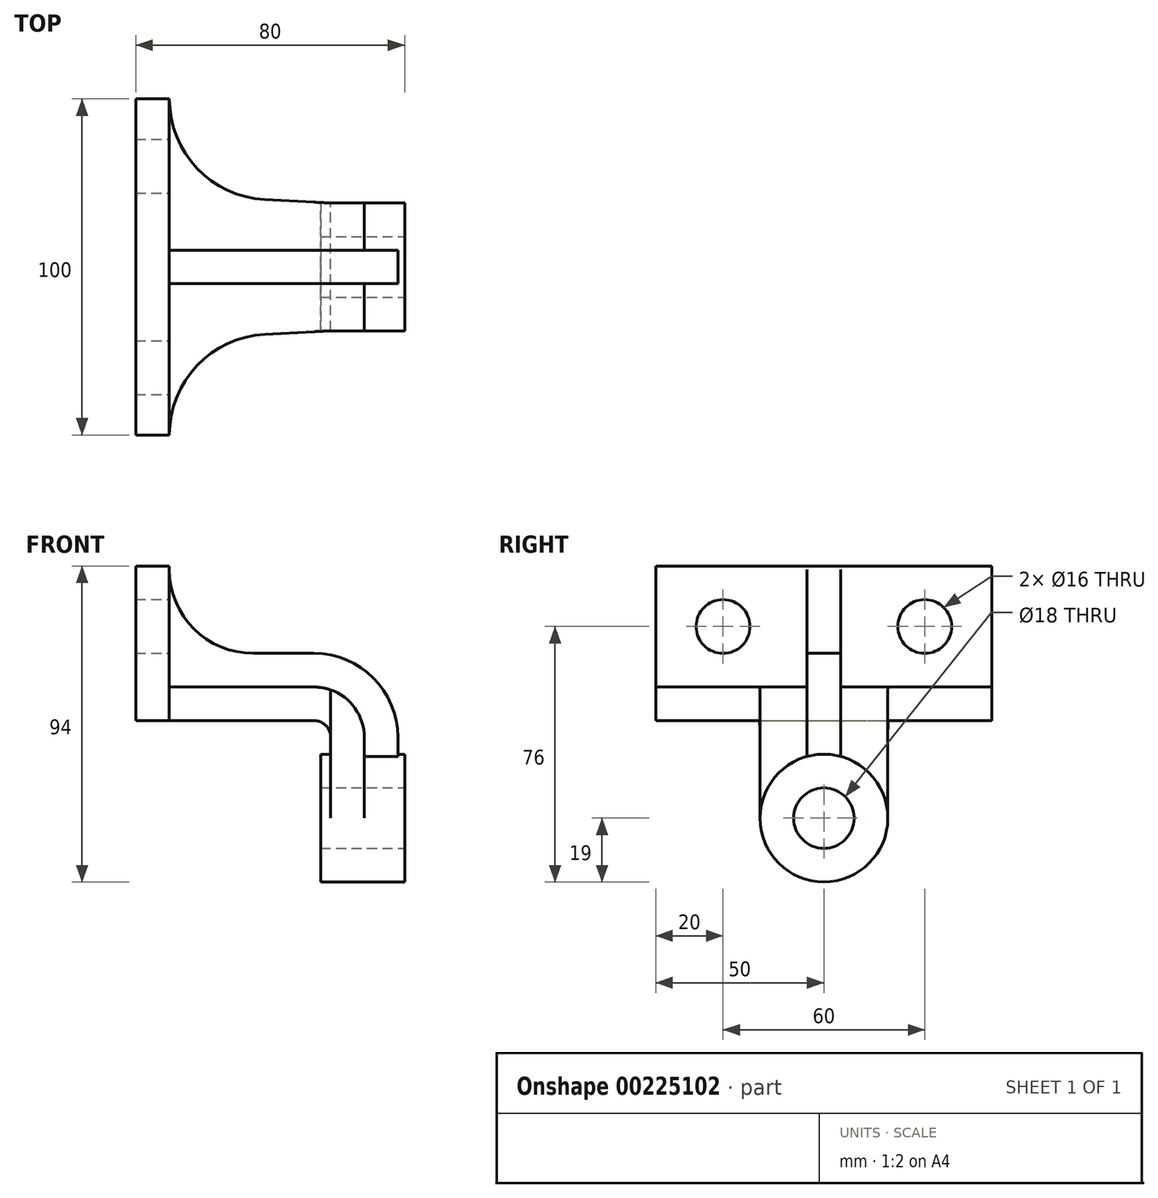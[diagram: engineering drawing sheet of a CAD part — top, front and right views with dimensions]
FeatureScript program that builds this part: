
annotation { "Feature Type Name" : "Feature", "Feature Type Description" : "" }
export const myFeature = defineFeature(function(context is Context, id is Id, definition is map)
    precondition{}
    {
        {
            var Q0;
            Q0=qCreatedBy(makeId("Front.planeOp"),FACE);
            var sketch = newSketch(context, id + "F0", { "sketchPlane" : qUnion([Q0])});
            skLineSegment(sketch, "E0", {"start": v(0, 0) * mm, "end": v(0, 46) * mm});
            skLineSegment(sketch, "E1", {"start": v(0, 46) * mm, "end": v(10, 46) * mm});
            skLineSegment(sketch, "E2", {"start": v(10, 46) * mm, "end": v(10, 10) * mm});
            skLineSegment(sketch, "E3", {"start": v(10, 10) * mm, "end": v(58, 10) * mm});
            skLineSegment(sketch, "E4", {"start": v(58, 10) * mm, "end": v(68, 10) * mm});
            skLineSegment(sketch, "E5", {"start": v(68, 10) * mm, "end": v(68, -29) * mm});
            skLineSegment(sketch, "E6", {"start": v(68, -29) * mm, "end": v(58, -29) * mm});
            skLineSegment(sketch, "E7", {"start": v(58, -29) * mm, "end": v(58, 10) * mm});
            skLineSegment(sketch, "E8", {"start": v(0, 0) * mm, "end": v(58, 0) * mm});
            skSolve(sketch);
        }
        {
            var Q0;
            Q0=makeQuery(id+"F0.imprint","IMPRINT",FACE,{"disambiguationData":[TD([[makeQuery(id+"F0.imprint","IMPRINT",EDGE,{"derivedFrom":sQuery(id+"F0.wireOp",EDGE,"E0")}),-1.0]])]});
            extrude(context, id + "F1", {"entities" : qUnion([Q0]), "endBound" : BoundingType.SYMMETRIC, "depth" : 100 * mm});
        }
        {
            var Q0;
            Q0 = qSketchRegion(id + "F0", true);
            extrude(context, id + "F2", {"entities" : qUnion([Q0]), "operationType" : NewBodyOperationType.ADD, "endBound" : BoundingType.SYMMETRIC, "depth" : 38 * mm});
        }
        {
            var Q0;
            {var subQ0=sQuery(id+"F0.wireOp",EDGE,"E3");Q0=makeQuery(id+"F2.boolean.opBoolean","MERGE",FACE,{"derivedFrom":[makeQuery(id+"F1.opExtrude","SWEPT_FACE",FACE,{"disambiguationData":[OSD([subQ0])]}),makeQuery(id+"F2.opExtrude","SWEPT_FACE",FACE,{"disambiguationData":[OSD([subQ0,sQuery(id+"F0.wireOp",EDGE,"E4")])]})]});}
            var sketch = newSketch(context, id + "F3", { "sketchPlane" : qUnion([Q0])});
            skLineSegment(sketch, "E9", {"start": v(-13.83, 0) * mm, "end": v(85.3, 0) * mm, "construction": true});
            skArc(sketch, "E10", {"start": v(38.4, -20.04) * mm, "mid": v(18.23, -29.36) * mm, "end": v(10, -50) * mm});
            skArc(sketch, "E11", {"start": v(10, 50) * mm, "mid": v(18.23, 29.36) * mm, "end": v(38.4, 20.04) * mm});
            skLineSegment(sketch, "E12", {"start": v(58, -19) * mm, "end": v(38.4, -20.04) * mm});
            skLineSegment(sketch, "E13", {"start": v(58, 19) * mm, "end": v(38.4, 20.04) * mm});
            skPoint(sketch, "E14.0", {"position": v(58, -34.5) * mm});
            skLineSegment(sketch, "E15.0", {"start": v(58, -50) * mm, "end": v(58, -19) * mm});
            skLineSegment(sketch, "E16.0.1", {"start": v(58, -19) * mm, "end": v(68, -19) * mm});
            skLineSegment(sketch, "E16.0.2", {"start": v(68, -19) * mm, "end": v(68, 19) * mm});
            skLineSegment(sketch, "E16.0.3", {"start": v(68, 19) * mm, "end": v(58, 19) * mm});
            skLineSegment(sketch, "E16.0.4", {"start": v(58, 19) * mm, "end": v(58, 50) * mm});
            skLineSegment(sketch, "E16.0.5", {"start": v(58, 50) * mm, "end": v(10, 50) * mm});
            skLineSegment(sketch, "E16.0.6", {"start": v(10, 50) * mm, "end": v(10, -50) * mm});
            skLineSegment(sketch, "E16.0.7", {"start": v(10, -50) * mm, "end": v(58, -50) * mm});
            skSolve(sketch);
        }
        {
            var Q0;
            Q0=makeQuery(id+"F3.imprint","IMPRINT",FACE,{"disambiguationData":[TD([[makeQuery(id+"F3.imprint","IMPRINT",EDGE,{"derivedFrom":sQuery(id+"F3.wireOp",EDGE,"E10")}),1.0]])]});
            var Q1;
            Q1=makeQuery(id+"F3.imprint","IMPRINT",FACE,{"disambiguationData":[TD([[makeQuery(id+"F3.imprint","IMPRINT",EDGE,{"derivedFrom":sQuery(id+"F3.wireOp",EDGE,"E11")}),1.0]])]});
            extrude(context, id + "F4", {"entities" : qUnion([Q0, Q1]), "operationType" : NewBodyOperationType.REMOVE, "endBound" : BoundingType.UP_TO_NEXT, "oppositeDirection" : true, "depth" : 25 * mm});
        }
        {
            var Q0;
            {var subQ0=sQuery(id+"F0.wireOp",EDGE,"E8");var subQ1=sQuery(id+"F0.wireOp",EDGE,"E7");Q0=makeQuery(id+"F2.boolean.opBoolean","MERGE",EDGE,{"derivedFrom":[makeQuery(id+"F1.opExtrude","SWEPT_EDGE",EDGE,{"disambiguationData":[OSD([subQ1,subQ0])]}),makeQuery(id+"F2.opExtrude","SWEPT_EDGE",EDGE,{"disambiguationData":[OSD([subQ1,subQ0])]})]});}
            fillet(context, id + "F5", {"entities" : qUnion([Q0]), "radius" : 5 * mm, "tangentPropagation" : true, "allowEdgeOverflow" : false});
        }
        {
            var Q0;
            Q0=makeQuery(id+"F2.opExtrude","SWEPT_EDGE",EDGE,{"disambiguationData":[OSD([sQuery(id+"F0.wireOp",EDGE,"E4"),sQuery(id+"F0.wireOp",EDGE,"E5")])]});
            fillet(context, id + "F6", {"entities" : qUnion([Q0]), "radius" : 15 * mm, "tangentPropagation" : true, "allowEdgeOverflow" : false});
        }
        {
            var Q0;
            Q0=makeQuery(id+"F1.opExtrude","SWEPT_FACE",FACE,{"disambiguationData":[OSD([sQuery(id+"F0.wireOp",EDGE,"E2")])]});
            var sketch = newSketch(context, id + "F7", { "sketchPlane" : qUnion([Q0])});
            skCircle(sketch, "E17", {"center": v(-30, 28) * mm, "radius": 8 * mm});
            skCircle(sketch, "E18", {"center": v(30, 28) * mm, "radius": 8 * mm});
            skSolve(sketch);
        }
        {
            var Q0;
            Q0 = qSketchRegion(id + "F7", true);
            extrude(context, id + "F8", {"entities" : qUnion([Q0]), "operationType" : NewBodyOperationType.REMOVE, "endBound" : BoundingType.UP_TO_NEXT, "oppositeDirection" : true, "depth" : 25 * mm});
        }
        {
            var Q0;
            Q0=qCreatedBy(makeId("Right.planeOp"),FACE);
            cPlane(context, id + "F9", {"entities" : qUnion([Q0]), "cplaneType" : CPlaneType.OFFSET, "offset" : 80 * mm, "width" : 150 * mm, "height" : 150 * mm});
        }
        {
            var Q0;
            Q0=qCreatedBy(id+"F9.planeOp",FACE);
            var sketch = newSketch(context, id + "F10", { "sketchPlane" : qUnion([Q0])});
            skCircle(sketch, "E19", {"center": v(0, -29) * mm, "radius": 19 * mm});
            skCircle(sketch, "E20", {"center": v(0, -29) * mm, "radius": 9 * mm});
            skLineSegment(sketch, "E21.0", {"start": v(19, -29) * mm, "end": v(19, -5) * mm});
            skLineSegment(sketch, "E22.0", {"start": v(-19, -29) * mm, "end": v(-19, -5) * mm});
            skLineSegment(sketch, "E23.0", {"start": v(-19, -29) * mm, "end": v(19, -29) * mm, "construction": true});
            skSolve(sketch);
        }
        {
            var Q0;
            Q0=qCreatedBy(makeId("Front.planeOp"),FACE);
            var sketch = newSketch(context, id + "F11", { "sketchPlane" : qUnion([Q0])});
            skArc(sketch, "E24", {"start": v(10.02, 45.88) * mm, "mid": v(17.01, 27.64) * mm, "end": v(35, 20) * mm});
            skArc(sketch, "E25", {"start": v(78, -5) * mm, "mid": v(70.68, 12.68) * mm, "end": v(53, 20) * mm});
            skLineSegment(sketch, "E26", {"start": v(35, 20) * mm, "end": v(53, 20) * mm});
            skLineSegment(sketch, "E27.0", {"start": v(10, 46) * mm, "end": v(10, 10) * mm});
            skLineSegment(sketch, "E28.0", {"start": v(0, 46) * mm, "end": v(10, 46) * mm});
            skPoint(sketch, "E29.0", {"position": v(18.23, 10) * mm});
            skLineSegment(sketch, "E30.0", {"start": v(38.4, 10) * mm, "end": v(10, 10) * mm});
            skLineSegment(sketch, "E31.0", {"start": v(53, 10) * mm, "end": v(38.4, 10) * mm});
            skArc(sketch, "E32.0", {"start": v(68, -5) * mm, "mid": v(65.25, 3.66) * mm, "end": v(58, 9.14) * mm});
            skPoint(sketch, "E33.0", {"position": v(55.54, 9.78) * mm});
            skLineSegment(sketch, "E34.0", {"start": v(68, -5) * mm, "end": v(68, -29) * mm});
            skLineSegment(sketch, "E35", {"start": v(68, -29) * mm, "end": v(78, -29) * mm});
            skLineSegment(sketch, "E36", {"start": v(78, -29) * mm, "end": v(78, -5) * mm});
            skLineSegment(sketch, "E37.0.0", {"start": v(0, 0) * mm, "end": v(10, 0) * mm});
            skLineSegment(sketch, "E37.0.1", {"start": v(10, 0) * mm, "end": v(10, 10) * mm});
            skLineSegment(sketch, "E37.0.2", {"start": v(10, 10) * mm, "end": v(10, 46) * mm});
            skLineSegment(sketch, "E37.0.3", {"start": v(10, 46) * mm, "end": v(0, 46) * mm});
            skLineSegment(sketch, "E37.0.4", {"start": v(0, 46) * mm, "end": v(0, 0) * mm});
            skLineSegment(sketch, "E38.0.0", {"start": v(10, 0) * mm, "end": v(38.4, 0) * mm});
            skLineSegment(sketch, "E38.0.1", {"start": v(38.4, 0) * mm, "end": v(38.4, 10) * mm});
            skLineSegment(sketch, "E38.0.3", {"start": v(10, 10) * mm, "end": v(10, 0) * mm});
            skArc(sketch, "E39.1", {"start": v(58, 9.14) * mm, "mid": v(55.54, 9.78) * mm, "end": v(53, 10) * mm});
            skSolve(sketch);
        }
        {
            var Q0;
            Q0 = qSketchRegion(id + "F11", true);
            extrude(context, id + "F12", {"entities" : qUnion([Q0]), "operationType" : NewBodyOperationType.ADD, "endBound" : BoundingType.SYMMETRIC, "depth" : 10 * mm});
        }
        {
            var Q0;
            Q0=makeQuery(id+"F10.imprint","IMPRINT",FACE,{"disambiguationData":[TD([[makeQuery(id+"F10.imprint","IMPRINT",EDGE,{"derivedFrom":sQuery(id+"F10.wireOp",EDGE,"E20")}),-1.0]])]});
            extrude(context, id + "F13", {"entities" : qUnion([Q0]), "operationType" : NewBodyOperationType.ADD, "oppositeDirection" : true, "depth" : 25 * mm});
        }
        {
            var Q0;
            {var subQ8=sQuery(id+"F11.wireOp",EDGE,"E36");Q0=makeQuery(id+"F13.boolean.opBoolean","SPLIT",FACE,{"disambiguationData":[TD([makeQuery(id+"F2.opExtrude","SWEPT_FACE",FACE,{"disambiguationData":[OSD([sQuery(id+"F0.wireOp",EDGE,"E6")])]})])],"derivedFrom":makeQuery(id+"F12.opExtrude","SWEPT_FACE",FACE,{"disambiguationData":[OSD([subQ8])]})});}
            var Q1;
            {var subQ0=sQuery(id+"F0.wireOp",EDGE,"E6");var subQ1=makeQuery(id+"F2.opExtrude","SWEPT_FACE",FACE,{"disambiguationData":[OSD([subQ0])]});var subQ5=sQuery(id+"F0.wireOp",EDGE,"E5");var subQ6=sQuery(id+"F0.wireOp",EDGE,"E4");Q1=makeQuery(id+"F13.boolean.opBoolean","SPLIT",FACE,{"disambiguationData":[TD([subQ1])],"derivedFrom":makeQuery(id+"F12.boolean.opBoolean","SPLIT",FACE,{"disambiguationData":[TD([makeQuery(id+"F2.opExtrude","CAP_FACE",FACE,{"disambiguationData":[OSD([sQuery(id+"F0.wireOp",EDGE,"E0"),sQuery(id+"F0.wireOp",EDGE,"E1"),sQuery(id+"F0.wireOp",EDGE,"E2"),sQuery(id+"F0.wireOp",EDGE,"E3"),subQ6,subQ5,subQ0,sQuery(id+"F0.wireOp",EDGE,"E7"),sQuery(id+"F0.wireOp",EDGE,"E8")])],"isStart":false})])],"derivedFrom":makeQuery(id+"F2.opExtrude","SWEPT_FACE",FACE,{"disambiguationData":[OSD([subQ5])]})})});}
            var Q2;
            {var subQ0=sQuery(id+"F0.wireOp",EDGE,"E6");var subQ1=makeQuery(id+"F2.opExtrude","SWEPT_FACE",FACE,{"disambiguationData":[OSD([subQ0])]});var subQ5=sQuery(id+"F0.wireOp",EDGE,"E5");var subQ6=sQuery(id+"F0.wireOp",EDGE,"E4");Q2=makeQuery(id+"F13.boolean.opBoolean","SPLIT",FACE,{"disambiguationData":[TD([subQ1])],"derivedFrom":makeQuery(id+"F12.boolean.opBoolean","SPLIT",FACE,{"disambiguationData":[TD([makeQuery(id+"F2.opExtrude","CAP_FACE",FACE,{"disambiguationData":[OSD([sQuery(id+"F0.wireOp",EDGE,"E0"),sQuery(id+"F0.wireOp",EDGE,"E1"),sQuery(id+"F0.wireOp",EDGE,"E2"),sQuery(id+"F0.wireOp",EDGE,"E3"),subQ6,subQ5,subQ0,sQuery(id+"F0.wireOp",EDGE,"E7"),sQuery(id+"F0.wireOp",EDGE,"E8")])],"isStart":true})])],"derivedFrom":makeQuery(id+"F2.opExtrude","SWEPT_FACE",FACE,{"disambiguationData":[OSD([subQ5])]})})});}
            extrude(context, id + "F14", {"entities" : qUnion([Q0, Q1, Q2]), "operationType" : NewBodyOperationType.REMOVE, "endBound" : BoundingType.UP_TO_NEXT, "oppositeDirection" : true, "depth" : 25 * mm});
        }
    });
